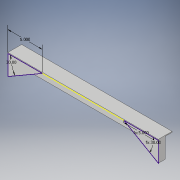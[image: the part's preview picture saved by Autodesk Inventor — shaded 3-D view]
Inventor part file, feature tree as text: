
AUTODESK INVENTOR PART (.ipt)
format: ipt  version: 2019 (Build 230136000, 136)  size: 121,856 bytes
history: native  units: in
note: dims shown in document units (in); Inventor stores cm internally (conversion verified against a paired STEP export)
features: extrude x4, sketch x3
ambient origin geometry x8: Origin, YZ Plane, XZ Plane, XY Plane, X Axis, Y Axis, Z Axis, Center Point
bodies: Solid1 (feature_tree)
feature tree (7):
  extrude  "Extrusion1"  Depth=2.0in
  sketch  "Sketch2"  dims[d2=0.12in d3=0.0in d6=5.0in]
  extrude  "Extrusion2"  Depth=0.12in
  extrude  "Extrusion3"  TaperAngle=30.0deg  [1 undecoded]
  extrude  "Extrusion4"  Depth=1.0in TaperAngle=0.0deg
  sketch  "Sketch1"  dims[d0=21.865in d1=2.0in]
  sketch  "Sketch3"  dims[d8=5.0in d9=30.0deg d10=1.0in d11=0.0in d12=1.0in d13=0.0in d15=30.0deg d16=14.5in d17=0.75in d18=0.0in]
note: 1 required parameter value undecoded (feature->parameter linkage not recoverable at this tier; creation-order binding heuristic only, values carry confidence <= 0.55)
